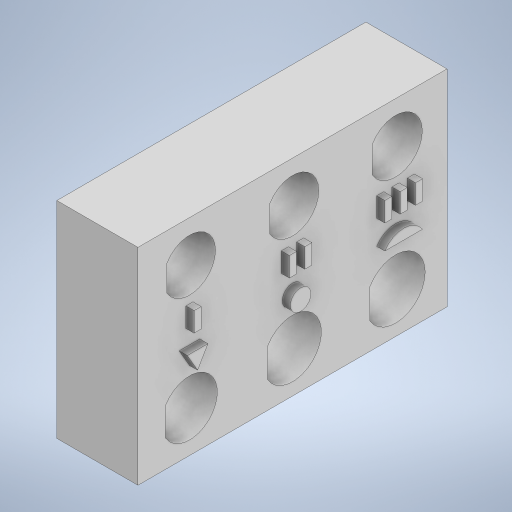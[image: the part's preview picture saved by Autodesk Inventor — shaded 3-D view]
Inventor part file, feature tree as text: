
AUTODESK INVENTOR PART (.ipt)
format: ipt  version: 2023 (Build 270158000, 158)  size: 345,600 bytes
history: native  units: in
note: dims shown in document units (in); Inventor stores cm internally (conversion verified against a paired STEP export)
features: extrude x2, sketch x1
ambient origin geometry x8: Origin, YZ Plane, XZ Plane, XY Plane, X Axis, Y Axis, Z Axis, Center Point
bodies: Solid1 (feature_tree)
feature tree (3):
  sketch  "Sketch1"  dims[d0=0.2525in d1=0.1263in d2=0.255in d3=0.1275in d4=0.26in d5=0.13in d6=0.27in d7=0.135in d8=0.28in d9=0.14in d10=0.2875in d11=0.1438in d12=1.5in d13=0.25in d14=0.25in d15=0.2in d16=1.0in d17=0.2in d18=0.0344in d19=0.0947in d20=0.09in d21=0.0344in d22=0.0947in d23=0.0344in d24=0.0947in d25=0.02in d26=0.02in d27=0.0344in d28=0.0947in d29=0.0344in d30=0.0947in d31=0.0344in d32=0.0947in d33=0.04in d35=0.04in d36=0.1in d38=0.1in d39=0.1in d40=0.035in d41=0.1in d42=0.075in d43=0.1833in d44=0.109in d45=0.224in d46=0.25in d47=0.3937in d48=0.0in d49=0.4331in d50=0.0in]
  extrude  "Extrusion1"  Depth=0.1275in
  extrude  "Extrusion2"  Depth=0.13in
